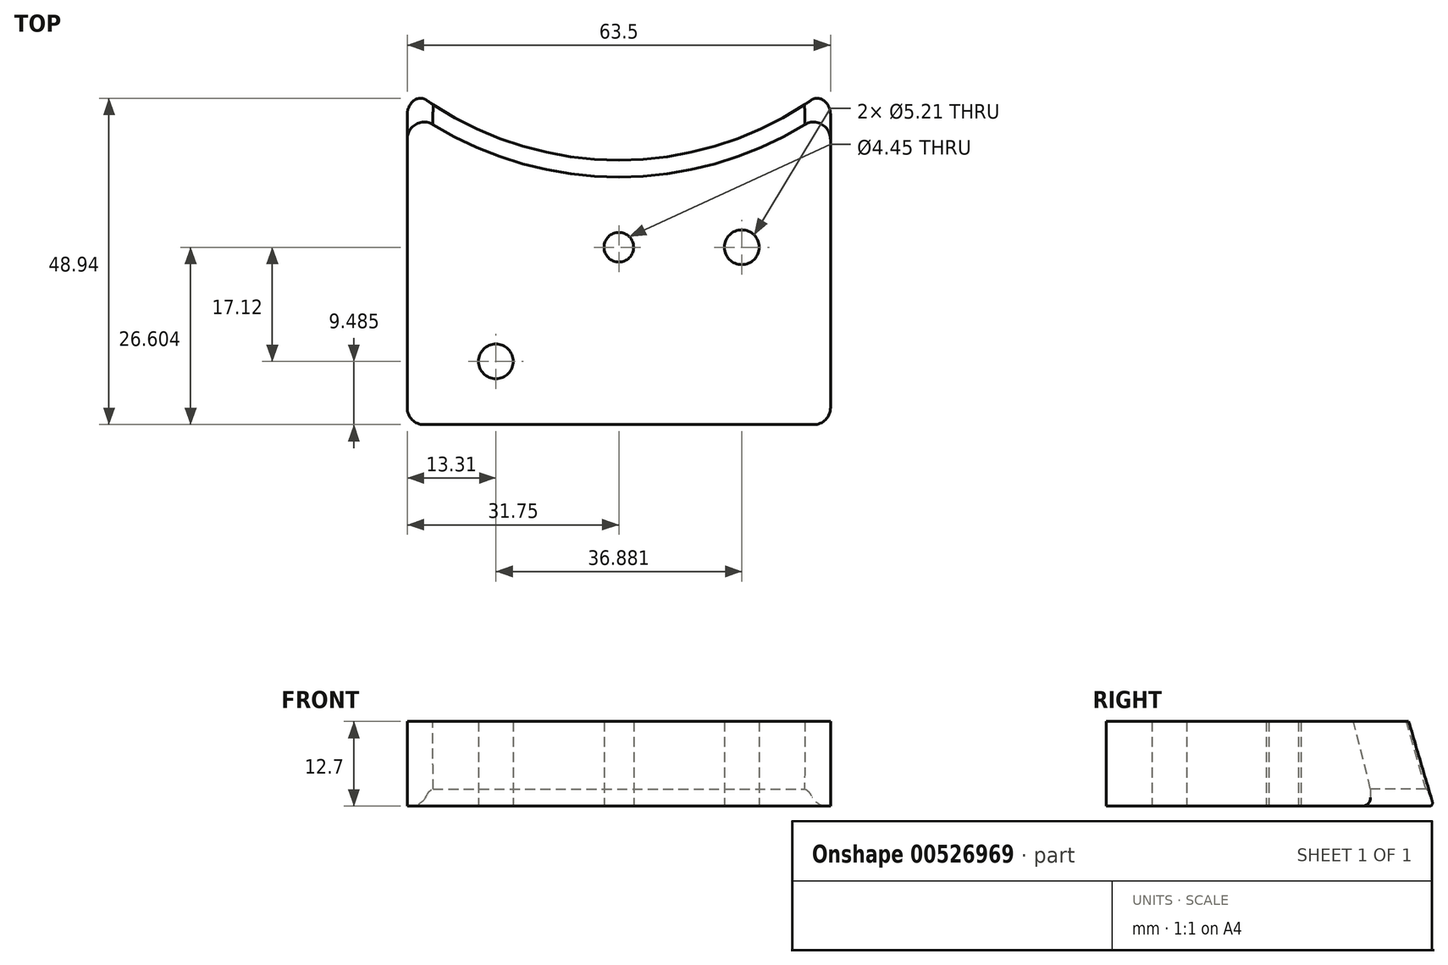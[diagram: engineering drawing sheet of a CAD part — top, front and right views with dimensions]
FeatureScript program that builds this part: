
annotation { "Feature Type Name" : "Feature", "Feature Type Description" : "" }
export const myFeature = defineFeature(function(context is Context, id is Id, definition is map)
    precondition{}
    {
        {
            var Q0;
            Q0=qCreatedBy(makeId("Top.planeOp"),FACE);
            var sketch = newSketch(context, id + "F0", { "sketchPlane" : qUnion([Q0])});
            skArc(sketch, "E0", {"start": v(-31.75, 11.14) * mm, "mid": v(0, 0) * mm, "end": v(31.75, 11.14) * mm});
            skLineSegment(sketch, "E1.bottom", {"start": v(31.75, -39.66) * mm, "end": v(-31.75, -39.66) * mm});
            skLineSegment(sketch, "E1.left", {"start": v(31.75, -39.66) * mm, "end": v(31.75, 11.14) * mm});
            skLineSegment(sketch, "E1.right", {"start": v(-31.75, -39.66) * mm, "end": v(-31.75, 11.14) * mm});
            skPoint(sketch, "E1.middle", {"position": v(0, -14) * mm});
            skCircle(sketch, "E2", {"center": v(0, -13.06) * mm, "radius": 2.22 * mm});
            skCircle(sketch, "E3", {"center": v(-18.44, -30.18) * mm, "radius": 2.6 * mm});
            skCircle(sketch, "E4", {"center": v(18.44, -13.06) * mm, "radius": 2.6 * mm});
            skSolve(sketch);
        }
        {
            var Q0;
            Q0=makeQuery(id+"F0.imprint","IMPRINT",FACE,{"disambiguationData":[TD([[makeQuery(id+"F0.imprint","IMPRINT",EDGE,{"derivedFrom":sQuery(id+"F0.wireOp",EDGE,"E0")}),-1.0]])]});
            extrude(context, id + "F1", {"entities" : qUnion([Q0]), "depth" : 12.7 * mm, "offsetDistance" : 25.4 * mm});
        }
        {
            var Q0;
            Q0=makeQuery(id+"F1.opExtrude","CAP_EDGE",EDGE,{"disambiguationData":[OSD([sQuery(id+"F0.wireOp",EDGE,"E0")])],"isStart":false});
            chamfer(context, id + "F2", {"entities" : qUnion([Q0]), "chamferType" : ChamferType.TWO_OFFSETS, "width1" : 10.16 * mm, "oppositeDirection" : false, "width2" : 2.54 * mm, "tangentPropagation" : true});
        }
        {
            var Q0;
            Q0=makeQuery(id+"F2.opChamfer","BLEND_EDGE",EDGE,{"blendedFrom":[makeQuery(id+"F1.opExtrude","CAP_EDGE",EDGE,{"disambiguationData":[OSD([sQuery(id+"F0.wireOp",EDGE,"E0")])],"isStart":false}),makeQuery(id+"F1.opExtrude","SWEPT_FACE",FACE,{"disambiguationData":[OSD([sQuery(id+"F0.wireOp",EDGE,"E1.right")])]})],"blendedInto":[makeQuery(id+"F1.opExtrude","SWEPT_FACE",FACE,{"disambiguationData":[OSD([sQuery(id+"F0.wireOp",EDGE,"E1.right")])]})]});
            var Q1;
            Q1=makeQuery(id+"F2.opChamfer","BLEND_EDGE",EDGE,{"blendedFrom":[makeQuery(id+"F1.opExtrude","CAP_EDGE",EDGE,{"disambiguationData":[OSD([sQuery(id+"F0.wireOp",EDGE,"E0")])],"isStart":false}),makeQuery(id+"F1.opExtrude","SWEPT_FACE",FACE,{"disambiguationData":[OSD([sQuery(id+"F0.wireOp",EDGE,"E1.left")])]})],"blendedInto":[makeQuery(id+"F1.opExtrude","SWEPT_FACE",FACE,{"disambiguationData":[OSD([sQuery(id+"F0.wireOp",EDGE,"E1.left")])]})]});
            fillet(context, id + "F3", {"entities" : qUnion([Q0, Q1]), "radius" : 2.54 * mm, "tangentPropagation" : true, "allowEdgeOverflow" : false});
        }
        {
            var Q0;
            Q0=makeQuery(id+"F1.opExtrude","SWEPT_EDGE",EDGE,{"disambiguationData":[OSD([sQuery(id+"F0.wireOp",EDGE,"E1.bottom"),sQuery(id+"F0.wireOp",EDGE,"E1.right")])]});
            var Q1;
            Q1=makeQuery(id+"F1.opExtrude","SWEPT_EDGE",EDGE,{"disambiguationData":[OSD([sQuery(id+"F0.wireOp",EDGE,"E1.bottom"),sQuery(id+"F0.wireOp",EDGE,"E1.left")])]});
            fillet(context, id + "F4", {"entities" : qUnion([Q0, Q1]), "radius" : 2.54 * mm, "tangentPropagation" : true, "allowEdgeOverflow" : false});
        }
        {
            var Q0;
            Q0=makeQuery(id+"F1.opExtrude","CAP_EDGE",EDGE,{"disambiguationData":[OSD([sQuery(id+"F0.wireOp",EDGE,"E0")])],"isStart":true});
            fillet(context, id + "F5", {"entities" : qUnion([Q0]), "radius" : 1.27 * mm, "tangentPropagation" : true, "allowEdgeOverflow" : false});
        }
    });
